# Revit family: HVAC_Heat-Pump_Enertech_CTC-EcoAir-406-408
name_source: partatom
category: Specialty Equipment
revit_build: Autodesk Revit 2018 (Build: 20190510_1515(x64)
units: mm (PartAtom-declared; Revit-internal decimal feet)

## family parameters
Always vertical = Yes
Cut with Voids When Loaded = No
OmniClass Number = 23.75.00.00
OmniClass Title = Climate Control (HVAC)
Part Type = Normal
Room Calculation Point = No
Round Connector Dimension = Use Diameter
Shared = No
Work Plane-Based = No

## types (4) — shared parameters
AssetType = Fixed
BIMObjectName = HVAC_Water-Heaters_Enertech_CTC-EcoAir-406-408
Brand = CTC
BrineSystem_Min_MaxPressure = 0.2 - 3.0 bar
CO2Equivalent = 3.902 tonnes
Capacity = Fixed
Category = Heat Pumps, Air-to-water
Color = grey
Description = CTC EcoAir 400, a series of on/off air-to-water heat pumps available in six sizes with outputs of 6-17 kW. Model: 406-420
DurationUnit = Year
EnergyClassHeatingWithControl = A++ / A+
EnergyClassHeatingWithoutControl = A++ / A+
HasProtectiveEarth = Yes
IP_Code = IP X4
IfcExportAs = IfcElectricalDeviceCommon
IfcExportType = HEATER
Manufacturer = Enertech AB
ManufacturerCountry = Sweden
ManufacturerName = Enertech AB
ManufacturerURL = https://ctc.se
Material = Steel/copper
MaxOperatingPressureThermalStore = 3 bar
NBSDescription = Air to water heat pumps
NBSReference = 90-40-40/320
Name = CTC-EcoAir-406-408
NominalCurrent = 0 A
NominalDepth = 545 mm
NominalFrequencyRange = 50 Hz
NominalHeight = 1080 mm  [stored 3.54331 ft]
NominalWidth = 1245 mm
PhaseAngle = 0.00°
PowerFactor = 0 W
ProductInformation = CTC EcoAir 400, a series of on/off air-to-water heat pumps available in six sizes with outputs of 6-17 kW. Model: 406-420
PumpMainMaterial = Stainless Steel
RefrigerantQuantity = 2.2 kg
RefrigerantType = R407C
Revision = 5
SCOPModerate = 3.9
Shape = Rectangular
Size = 545x1245x1080 mm
Touchscreen = no
UNSPSCCode = 40101806
URL = https://ctc-heating.com
Uniclass2 = Pr_40_70_65
Uniclass2015Description = Preparation catering equipment
Uniclass2015Reference = Pr_40_70_65
UsageCurrent = 0 A
Version = 1
VersionDate = 26/08/2021
WarrantyDurationUnit = Year
zero-valued in all types: Cost

## per-type parameters (varying)
| type | AirFlow | COP | EANNumber | InPutPower | MaxStartingCurrent | Model | ModelNumber | NominalVoltage | NumberOfPoles | RatedCurrent | RatedHeatOutputModerate | RatedVoltage | SCOPCold | SCOPWarm | Sound pressureLPA 10m | Sound pressureLPA 5m | SoundPowerLWA | SpecifiedOutput | WaterVolumeHeathingSystem | Weight |
| CTC EcoAir 406 - 400V3N | 2500 m3/h | 4.78 | 7333077000059 | 1.3 kW | 11.9 A | CTC EcoAir 406 | 585600001 | 400 V | 3 | 4 A | 5 kW | 1200 V | 3.4 | 4.8 | 31 dB | 37 dB | 56 dB | 6.2 kW | 1.9 liters | 130 |
| CTC EcoAir 408 - 400V3N | 2800 m3/h | 4.83 | 7333077000066 | 1.6 kW | 10.8 A | CTC EcoAir 408 | 585600002 | 400 V | 3 | 5 A | 6 kW | 1200 V | 3.4 | 4.9 | 33 dB | 39 dB | 58 dB | 7.8 kW | 2.4 liters | 150 |
| CTC EcoAir 406 - 230V1N | 2500 m3/h | 4.78 | 7333077000103 | 1.3 kW | 22.8 A | CTC EcoAir 406 | 585600011 | 230 V | 1 | 10 A | 5 kW | 230 V | 3.5 | 4.8 | 31 dB | 37 dB | 56 dB | 6.2 kW | 1.9 liters | 130 |
| CTC EcoAir 408 - 230V1N | 2800 m3/h | 4.83 | 7333077000110 | 1.6 kW | 23.2 A | CTC EcoAir 408 | 585600012 | 230 V | 1 | 12 A |  | 230 V | 3.4 | 4.9 | 33 dB | 39 dB | 58 dB | 7.8 kW | 2.4 liters | 150 |

note: [stored X ft] marks values corroborated as IEEE doubles in the binary element streams (Revit-internal decimal feet)

## geometry (parser evidence)
native form markers: Sweep x5
no freeform markers — native parametric forms only
